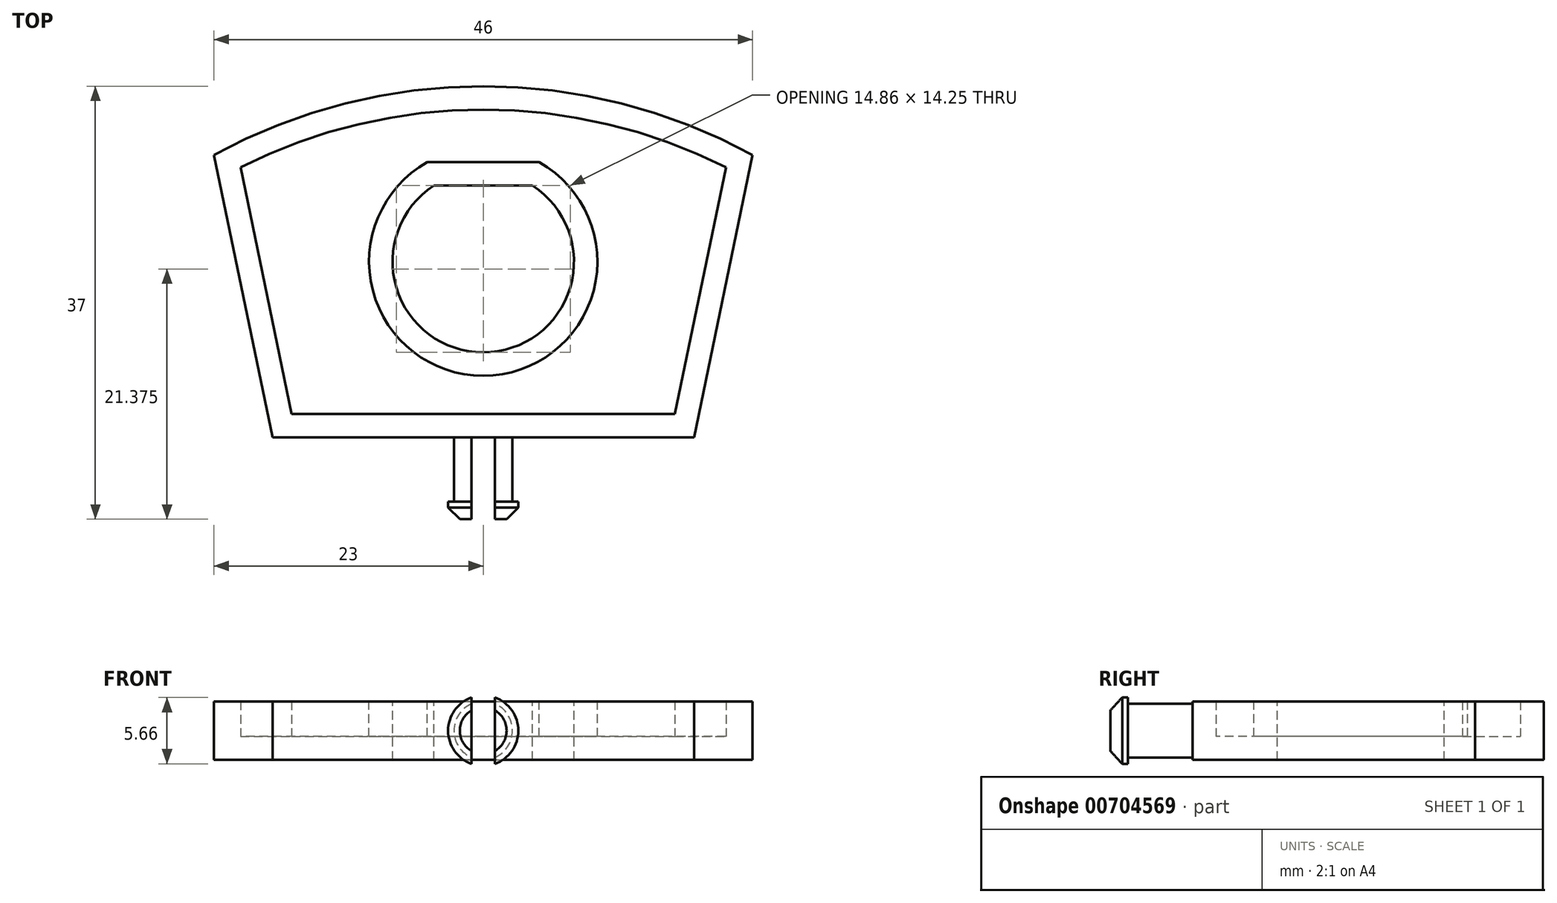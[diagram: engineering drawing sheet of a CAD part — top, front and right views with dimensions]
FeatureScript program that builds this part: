
annotation { "Feature Type Name" : "Feature", "Feature Type Description" : "" }
export const myFeature = defineFeature(function(context is Context, id is Id, definition is map)
    precondition{}
    {
        {
            var Q0;
            Q0=qCreatedBy(makeId("Top.planeOp"),FACE);
            var sketch = newSketch(context, id + "F0", { "sketchPlane" : qUnion([Q0])});
            skLineSegment(sketch, "E0", {"start": v(-23, 24.13) * mm, "end": v(-18, 0) * mm});
            skLineSegment(sketch, "E1", {"start": v(-18, 0) * mm, "end": v(18, 0) * mm});
            skLineSegment(sketch, "E2", {"start": v(18, 0) * mm, "end": v(23, 24.13) * mm});
            skArc(sketch, "E3", {"start": v(23, 24.13) * mm, "mid": v(0, 30) * mm, "end": v(-23, 24.13) * mm});
            skSolve(sketch);
        }
        {
            var Q0;
            Q0 = qSketchRegion(id + "F0", true);
            extrude(context, id + "F1", {"entities" : qUnion([Q0]), "endBound" : BoundingType.SYMMETRIC, "depth" : 5 * mm, "offsetDistance" : 25 * mm});
        }
        {
            var Q0;
            Q0=makeQuery(id+"F1.opExtrude","CAP_FACE",FACE,{"disambiguationData":[OSD([sQuery(id+"F0.wireOp",EDGE,"E0"),sQuery(id+"F0.wireOp",EDGE,"E1"),sQuery(id+"F0.wireOp",EDGE,"E2"),sQuery(id+"F0.wireOp",EDGE,"E3")])],"isStart":false});
            var sketch = newSketch(context, id + "F2", { "sketchPlane" : qUnion([Q0])});
            skLineSegment(sketch, "E4", {"start": v(-4.22, 21.5) * mm, "end": v(4.22, 21.5) * mm});
            skArc(sketch, "E5", {"start": v(-4.22, 21.5) * mm, "mid": v(0, 7.25) * mm, "end": v(4.22, 21.5) * mm});
            skSolve(sketch);
        }
        {
            var Q0;
            Q0 = qSketchRegion(id + "F2", true);
            var Q1;
            Q1=makeQuery(id+"F2.imprint","IMPRINT",FACE,{"disambiguationData":[TD([[makeQuery(id+"F2.imprint","IMPRINT",EDGE,{"derivedFrom":sQuery(id+"F2.wireOp",EDGE,"E4")}),-1.0]])]});
            extrude(context, id + "F3", {"entities" : qUnion([Q0, Q1]), "operationType" : NewBodyOperationType.ADD, "depth" : 25 * mm, "offsetDistance" : 25 * mm});
        }
        {
            var Q0;
            Q0=makeQuery(id+"F3.opExtrude","CAP_FACE",FACE,{"disambiguationData":[OSD([sQuery(id+"F2.wireOp",EDGE,"E4"),sQuery(id+"F2.wireOp",EDGE,"E5")])],"isStart":false});
            extrude(context, id + "F4", {"entities" : qUnion([Q0]), "operationType" : NewBodyOperationType.REMOVE, "endBound" : BoundingType.UP_TO_NEXT, "oppositeDirection" : true, "depth" : 25 * mm, "offsetDistance" : 25 * mm});
        }
        {
            var Q0;
            Q0=makeQuery(id+"F1.opExtrude","CAP_FACE",FACE,{"disambiguationData":[OSD([sQuery(id+"F0.wireOp",EDGE,"E0"),sQuery(id+"F0.wireOp",EDGE,"E1"),sQuery(id+"F0.wireOp",EDGE,"E2"),sQuery(id+"F0.wireOp",EDGE,"E3")])],"isStart":false});
            shell(context, id + "F5", {"entities" : qUnion([Q0]), "thickness" : 2 * mm});
        }
        {
            var Q0;
            Q0=qCreatedBy(makeId("Right.planeOp"),FACE);
            var sketch = newSketch(context, id + "F6", { "sketchPlane" : qUnion([Q0])});
            skLineSegment(sketch, "E6", {"start": v(0, 0) * mm, "end": v(-7, 0) * mm});
            skLineSegment(sketch, "E7", {"start": v(-7, 0) * mm, "end": v(-7, 3) * mm});
            skLineSegment(sketch, "E8", {"start": v(-7, 3) * mm, "end": v(-5.5, 3) * mm});
            skLineSegment(sketch, "E9", {"start": v(-5.5, 3) * mm, "end": v(-5.5, 2.5) * mm});
            skLineSegment(sketch, "E10", {"start": v(-5.5, 2.5) * mm, "end": v(0, 2.5) * mm});
            skLineSegment(sketch, "E11", {"start": v(0, 2.5) * mm, "end": v(0, 0) * mm});
            skSolve(sketch);
        }
        {
            var Q0;
            Q0=makeQuery(id+"F6.imprint","IMPRINT",FACE,{"disambiguationData":[TD([[makeQuery(id+"F6.imprint","IMPRINT",EDGE,{"derivedFrom":sQuery(id+"F6.wireOp",EDGE,"E6")}),-1.0]])]});
            var Q1;
            Q1=sQuery(id+"F6.wireOp",EDGE,"E6");
            revolve(context, id + "F7", {"operationType" : NewBodyOperationType.ADD, "surfaceOperationType" : NewSurfaceOperationType.NEW, "entities" : qUnion([Q0]), "axis" : qUnion([Q1]), "revolveType" : RevolveType.FULL});
        }
        {
            var Q0;
            Q0=makeQuery(id+"F7.opRevolve","SWEPT_EDGE",EDGE,{"disambiguationData":[OSD([sQuery(id+"F6.wireOp",EDGE,"E7"),sQuery(id+"F6.wireOp",EDGE,"E8")])]});
            chamfer(context, id + "F8", {"entities" : qUnion([Q0]), "width" : 1 * mm, "tangentPropagation" : true});
        }
        {
            var Q0;
            Q0=qCreatedBy(makeId("Front.planeOp"),FACE);
            var sketch = newSketch(context, id + "F9", { "sketchPlane" : qUnion([Q0])});
            skLineSegment(sketch, "E12.bottom", {"start": v(1, 3.5) * mm, "end": v(-1, 3.5) * mm});
            skLineSegment(sketch, "E12.top", {"start": v(1, -3.5) * mm, "end": v(-1, -3.5) * mm});
            skLineSegment(sketch, "E12.left", {"start": v(1, 3.5) * mm, "end": v(1, -3.5) * mm});
            skLineSegment(sketch, "E12.right", {"start": v(-1, 3.5) * mm, "end": v(-1, -3.5) * mm});
            skPoint(sketch, "E12.middle", {"position": v(0, 0) * mm});
            skSolve(sketch);
        }
        {
            var Q0;
            Q0 = qSketchRegion(id + "F9", true);
            extrude(context, id + "F10", {"entities" : qUnion([Q0]), "operationType" : NewBodyOperationType.REMOVE, "depth" : 8 * mm, "offsetDistance" : 25 * mm});
        }
    });
